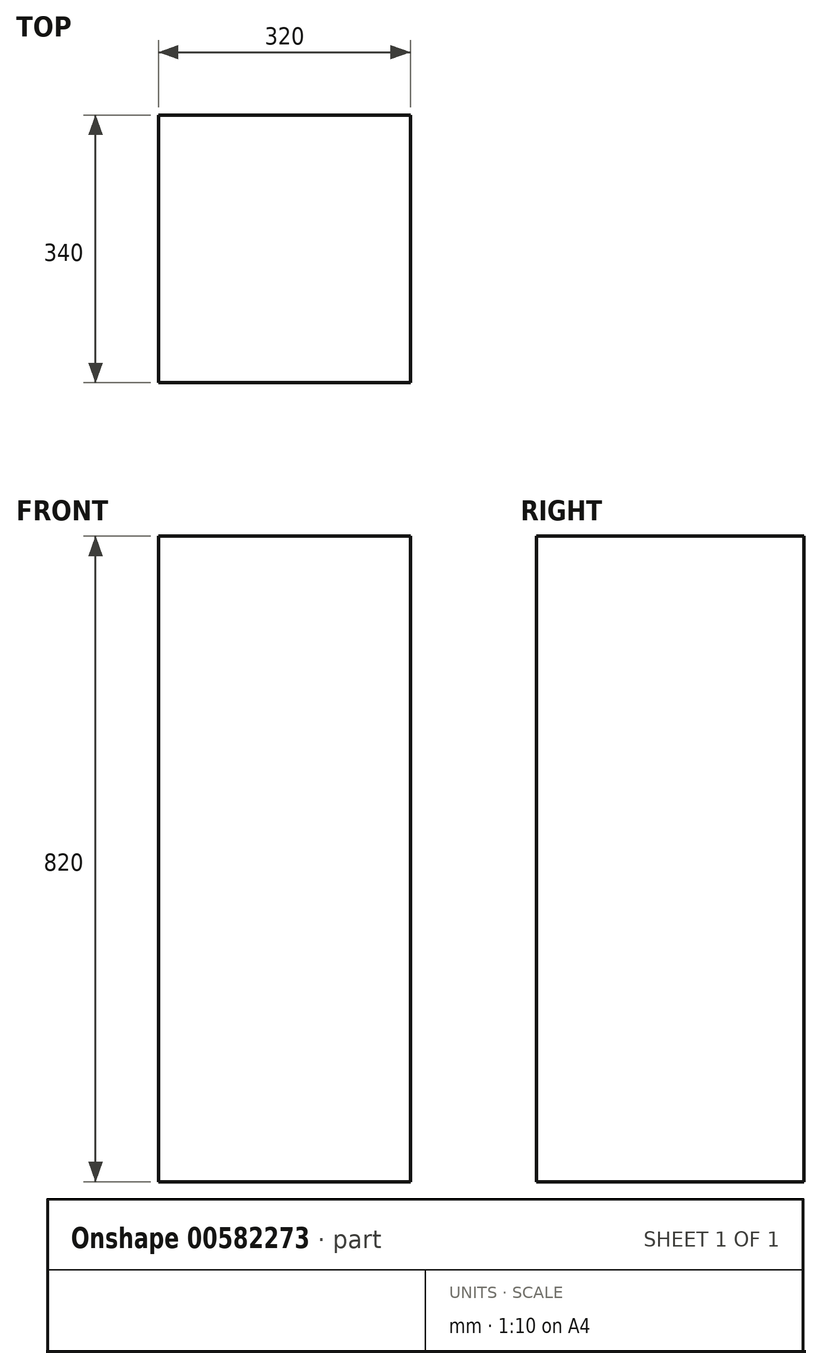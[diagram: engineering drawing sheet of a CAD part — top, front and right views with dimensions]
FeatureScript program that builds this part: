
annotation { "Feature Type Name" : "Feature", "Feature Type Description" : "" }
export const myFeature = defineFeature(function(context is Context, id is Id, definition is map)
    precondition{}
    {
        {
            var Q0;
            Q0=qCreatedBy(makeId("Front.planeOp"),FACE);
            var sketch = newSketch(context, id + "F0", { "sketchPlane" : qUnion([Q0])});
            skLineSegment(sketch, "E0.bottom", {"start": v(0, 0) * mm, "end": v(320, 0) * mm});
            skLineSegment(sketch, "E0.top", {"start": v(0, 820) * mm, "end": v(320, 820) * mm});
            skLineSegment(sketch, "E0.left", {"start": v(0, 0) * mm, "end": v(0, 820) * mm});
            skLineSegment(sketch, "E0.right", {"start": v(320, 0) * mm, "end": v(320, 820) * mm});
            skSolve(sketch);
        }
        {
            var Q0;
            Q0=makeQuery(id+"F0.imprint","IMPRINT",FACE,{"disambiguationData":[TD([[makeQuery(id+"F0.imprint","IMPRINT",EDGE,{"derivedFrom":sQuery(id+"F0.wireOp",EDGE,"E0.bottom")}),1.0]])]});
            extrude(context, id + "F1", {"entities" : qUnion([Q0]), "depth" : 340 * mm, "offsetDistance" : 25 * mm});
        }
    });
